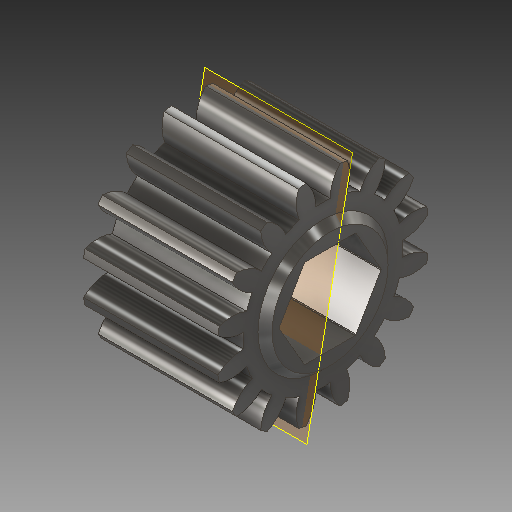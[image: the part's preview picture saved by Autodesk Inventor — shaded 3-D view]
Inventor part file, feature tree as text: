
AUTODESK INVENTOR PART (.ipt)
format: ipt  version: 2018 (Build 220112000, 112)  size: 313,856 bytes
history: native  units: in
note: dims shown in document units (in); Inventor stores cm internally (conversion verified against a paired STEP export)
features: plane x1, other x1
ambient origin geometry x8: Origin, YZ Plane, XZ Plane, XY Plane, X Axis, Y Axis, Z Axis, Center Point
bodies: Solid1 (feature_tree)
feature tree (2):
  plane  "Work Plane1"
  other  "Bore"
